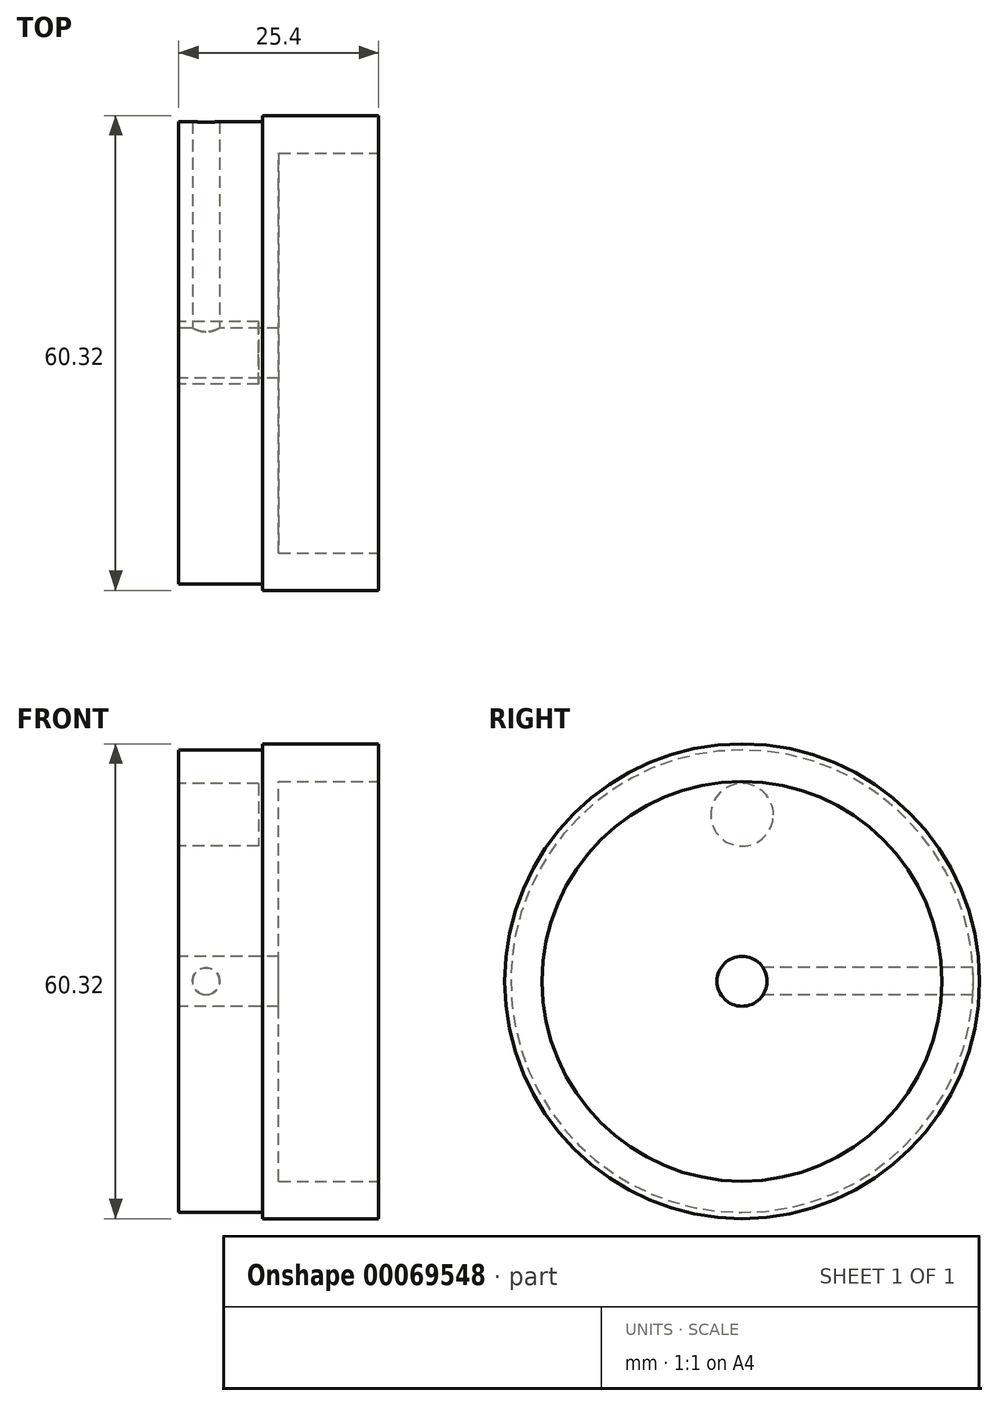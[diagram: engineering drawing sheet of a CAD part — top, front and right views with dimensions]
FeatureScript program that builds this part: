
annotation { "Feature Type Name" : "Feature", "Feature Type Description" : "" }
export const myFeature = defineFeature(function(context is Context, id is Id, definition is map)
    precondition{}
    {
        {
            var Q0;
            Q0=qCreatedBy(makeId("Front.planeOp"),FACE);
            var sketch = newSketch(context, id + "F0", { "sketchPlane" : qUnion([Q0])});
            skLineSegment(sketch, "E0", {"start": v(-51.58, 0) * mm, "end": v(-51.58, 29.38) * mm});
            skLineSegment(sketch, "E1", {"start": v(-51.58, 29.38) * mm, "end": v(-40.9, 29.38) * mm});
            skLineSegment(sketch, "E2", {"start": v(-40.9, 30.16) * mm, "end": v(-40.9, 29.38) * mm});
            skLineSegment(sketch, "E3", {"start": v(-40.9, 30.16) * mm, "end": v(-26.18, 30.16) * mm});
            skLineSegment(sketch, "E4", {"start": v(-26.18, 30.16) * mm, "end": v(-26.18, 0) * mm});
            skLineSegment(sketch, "E5", {"start": v(-26.18, 0) * mm, "end": v(-51.58, 0) * mm});
            skSolve(sketch);
        }
        {
            var Q0;
            Q0=makeQuery(id+"F0.imprint","IMPRINT",FACE,{"disambiguationData":[TD([[makeQuery(id+"F0.imprint","IMPRINT",EDGE,{"derivedFrom":sQuery(id+"F0.wireOp",EDGE,"E0")}),-1.0]])]});
            var Q1;
            Q1=sQuery(id+"F0.wireOp",EDGE,"E0");
            var Q2;
            Q2=sQuery(id+"F0.wireOp",EDGE,"E5");
            var Q3;
            Q3=sQuery(id+"F0.wireOp",EDGE,"E4");
            var Q4;
            Q4=sQuery(id+"F0.wireOp",EDGE,"E3");
            var Q5;
            Q5=sQuery(id+"F0.wireOp",EDGE,"E2");
            var Q6;
            Q6=sQuery(id+"F0.wireOp",EDGE,"E1");
            var Q7;
            Q7=sQuery(id+"F0.wireOp",EDGE,"E5");
            revolve(context, id + "F1", {"entities" : qUnion([Q0]), "surfaceEntities" : qUnion([Q1, Q2, Q3, Q4, Q5, Q6]), "axis" : qUnion([Q7]), "revolveType" : RevolveType.FULL});
        }
        {
            var Q0;
            Q0=makeQuery(id+"F1.opRevolve","SWEPT_FACE",FACE,{"disambiguationData":[OSD([sQuery(id+"F0.wireOp",EDGE,"E4")])]});
            var sketch = newSketch(context, id + "F2", { "sketchPlane" : qUnion([Q0])});
            skCircle(sketch, "E6", {"center": v(0, 0) * mm, "radius": 25.4 * mm});
            skSolve(sketch);
        }
        {
            var Q0;
            Q0=makeQuery(id+"F2.imprint","IMPRINT",FACE,{"disambiguationData":[TD([[makeQuery(id+"F2.imprint","IMPRINT",EDGE,{"derivedFrom":sQuery(id+"F2.wireOp",EDGE,"E6")}),1.0]])]});
            extrude(context, id + "F3", {"entities" : qUnion([Q0]), "operationType" : NewBodyOperationType.REMOVE, "oppositeDirection" : true, "depth" : 12.7 * mm});
        }
        {
            var Q0;
            Q0=makeQuery(id+"F1.opRevolve","SWEPT_FACE",FACE,{"disambiguationData":[OSD([sQuery(id+"F0.wireOp",EDGE,"E0")])]});
            var sketch = newSketch(context, id + "F4", { "sketchPlane" : qUnion([Q0])});
            skCircle(sketch, "E7", {"center": v(0, 0) * mm, "radius": 3.18 * mm});
            skSolve(sketch);
        }
        {
            var Q0;
            Q0=makeQuery(id+"F4.imprint","IMPRINT",FACE,{"disambiguationData":[TD([[makeQuery(id+"F4.imprint","IMPRINT",EDGE,{"derivedFrom":sQuery(id+"F4.wireOp",EDGE,"E7")}),1.0]])]});
            extrude(context, id + "F5", {"entities" : qUnion([Q0]), "operationType" : NewBodyOperationType.REMOVE, "oppositeDirection" : true, "depth" : 25.4 * mm});
        }
        {
            var Q0;
            Q0=makeQuery(id+"F1.opRevolve","SWEPT_FACE",FACE,{"disambiguationData":[OSD([sQuery(id+"F0.wireOp",EDGE,"E0")])]});
            var sketch = newSketch(context, id + "F6", { "sketchPlane" : qUnion([Q0])});
            skCircle(sketch, "E8", {"center": v(0, 21.15) * mm, "radius": 3.98 * mm});
            skSolve(sketch);
        }
        {
            var Q0;
            Q0=makeQuery(id+"F6.imprint","IMPRINT",FACE,{"disambiguationData":[TD([[makeQuery(id+"F6.imprint","IMPRINT",EDGE,{"derivedFrom":sQuery(id+"F6.wireOp",EDGE,"E8")}),1.0]])]});
            extrude(context, id + "F7", {"entities" : qUnion([Q0]), "operationType" : NewBodyOperationType.REMOVE, "oppositeDirection" : true, "depth" : 10.16 * mm});
        }
        {
            var Q0;
            Q0=qCreatedBy(makeId("Front.planeOp"),FACE);
            var sketch = newSketch(context, id + "F8", { "sketchPlane" : qUnion([Q0])});
            skCircle(sketch, "E9", {"center": v(-48.1, 0) * mm, "radius": 1.73 * mm});
            skSolve(sketch);
        }
        {
            var Q0;
            Q0 = qSketchRegion(id + "F8", true);
            extrude(context, id + "F9", {"entities" : qUnion([Q0]), "operationType" : NewBodyOperationType.REMOVE, "oppositeDirection" : true, "depth" : 70.56 * mm});
        }
    });
